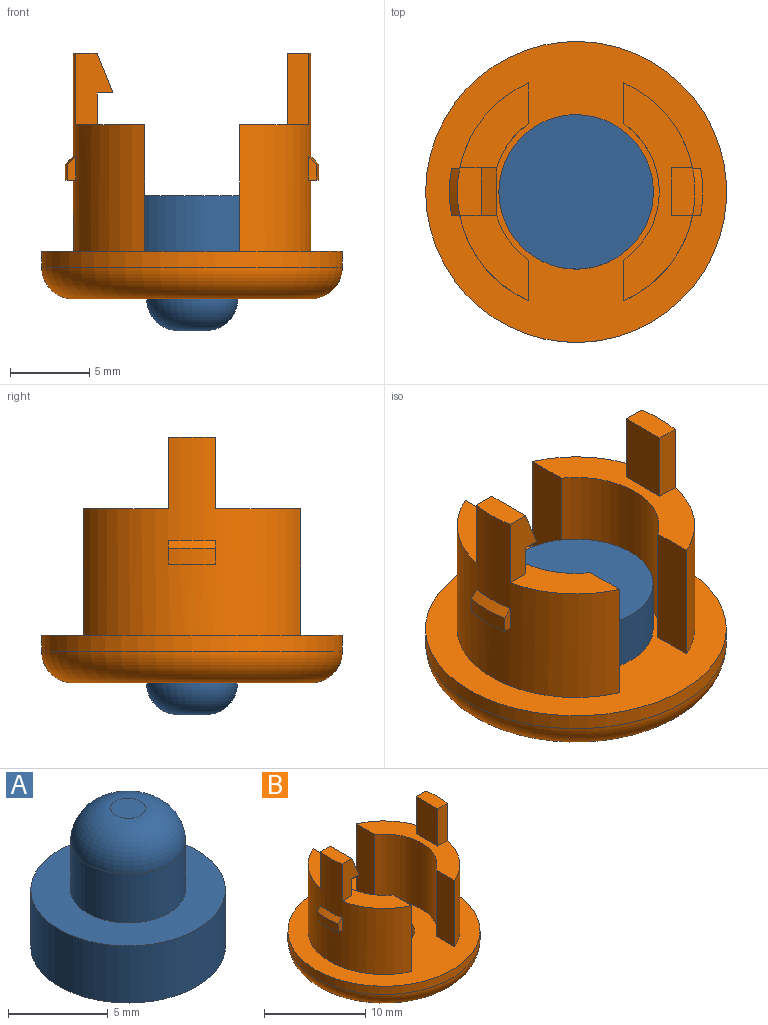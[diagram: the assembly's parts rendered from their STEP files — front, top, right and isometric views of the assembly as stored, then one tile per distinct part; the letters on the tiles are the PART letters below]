
ASSEMBLY  parts=2 mates=1
PART A: 6 faces, bbox 9.8x9.8x8.5 mm
  f0: cylinder r=4.88mm len=9.75mm, axis (0,0,-1), area 107.2mm2, adj f1,f2
  f1: plane 9.75x9.75mm, normal (0,0,1), area 48.7mm2, adj f0,f3
  f2: plane 9.75x9.75mm, normal (0,0,-1), area 74.7mm2, adj f0
  f3: cylinder r=2.88mm len=5.75mm, axis (0,0,-1), area 54.2mm2, adj f1,f5
  f4: plane 1.75x1.75mm, normal (0,0,1), area 2.4mm2, adj f5
  f5: torus R=0.88mm, axis (0,0,1), area 42.4mm2, adj f3,f4
PART B: 35 faces, bbox 20.6x20.6x15.5 mm
  f0: plane 3x2mm, normal (1,0,0), area 6mm2, adj f2,f26,f27,f33
  f1: plane 13.75x4.35mm, normal (0,0,1), area 26.6mm2, adj f3,f4,f12,f14,f29,f30,f31
  f2: plane 13.75x4.35mm, normal (0,0,1), area 26.6mm2, adj f0,f5,f6,f13,f15,f26,f27
  f3: cylinder r=5.25mm len=8.62mm, axis (0,0,-1), area 80.9mm2, adj f1,f7,f12,f14
  f4: cylinder r=7.5mm len=13.75mm, axis (0,0,-1), area 148.2mm2, adj f1,f7,f12,f14,f20,f21,f23,f24
  f5: cylinder r=5.25mm len=8.62mm, axis (0,0,-1), area 80.9mm2, adj f2,f7,f13,f15
  f6: cylinder r=7.5mm len=13.75mm, axis (0,0,-1), area 148.2mm2, adj f2,f7,f13,f15,f16,f18,f19,f25
  f7: plane 19x19mm, normal (0,0,1), area 193.3mm2, adj f3,f4,f5,f6,f8,f9,f12,f13
  f8: cylinder r=9.5mm len=19mm, axis (0,0,1), area 59.7mm2, adj f7,f11
  f9: cylinder r=3mm len=6mm, axis (0,0,1), area 56.5mm2, adj f7,f10
  f10: plane 15x15mm, normal (0,0,-1), area 148.4mm2, adj f9,f11
  f11: torus R=7.5mm, axis (0,0,-1), area 173.2mm2, adj f8,f10
  f12: plane 8x2.57mm, normal (-1,0,0), area 20.5mm2, adj f1,f3,f4,f7
  f13: plane 8x2.57mm, normal (1,0,0), area 20.5mm2, adj f2,f5,f6,f7
  f14: plane 8x2.57mm, normal (-1,0,0), area 20.5mm2, adj f1,f3,f4,f7
  f15: plane 8x2.57mm, normal (1,0,0), area 20.5mm2, adj f2,f5,f6,f7
  f16: plane 1.5x0.51mm, normal (0,1,0), area 0.6mm2, adj f6,f17,f19,f25
  f17: cylinder r=8mm len=3mm, axis (0,0,-1), area 3mm2, adj f16,f18,f19,f25
  f18: plane 1.5x0.51mm, normal (0,-1,0), area 0.6mm2, adj f6,f17,f19,f25
  f19: plane 3x0.65mm, normal (0,0,-1), area 1.5mm2, adj f6,f16,f17,f18
  f20: plane 1.5x0.51mm, normal (0,1,0), area 0.6mm2, adj f4,f22,f23,f24
  f21: plane 1.5x0.51mm, normal (0,-1,0), area 0.6mm2, adj f4,f22,f23,f24
  f22: cylinder r=8mm len=3mm, axis (0,0,-1), area 3mm2, adj f20,f21,f23,f24
  f23: plane 3x0.65mm, normal (0,0,-1), area 1.5mm2, adj f4,f20,f21,f22
  f24: cone r=7.5mm half-angle=45deg, axis (0,0,-1), area 2.1mm2, adj f4,f20,f21,f22
  f25: cone r=7.5mm half-angle=45deg, axis (0,0,-1), area 2.1mm2, adj f6,f16,f17,f18
  f26: plane 4.5x2.35mm, normal (0,1,0), area 7.3mm2, adj f0,f2,f6,f28,f33,f34
  f27: plane 4.5x2.35mm, normal (0,-1,0), area 7.3mm2, adj f0,f2,f6,f28,f33,f34
  f28: plane 3x1.5mm, normal (0,0,1), area 4.3mm2, adj f6,f26,f27,f34
  f29: plane 4.5x1.35mm, normal (0,-1,0), area 6.1mm2, adj f1,f4,f31,f32
  f30: plane 4.5x1.35mm, normal (0,1,0), area 6.1mm2, adj f1,f4,f31,f32
  f31: plane 4.5x3mm, normal (-1,0,0), area 13.5mm2, adj f1,f29,f30,f32
  f32: plane 3x1.5mm, normal (0,0,1), area 4.3mm2, adj f4,f29,f30,f31
  f33: plane 3x1mm, normal (0,0,-1), area 3mm2, adj f0,f26,f27,f34
  f34: plane 3x2.5mm, normal (0.93,0,0.37), area 8.1mm2, adj f26,f27,f28,f33
PLACE A rot(axis=(0,1,0),180deg) t=(0,0,6.5)mm
PLACE B t=(0,0,3)mm
MATE fastened A.f3 <-> B.f9  axis (0,0,-1) through (0,0,3)mm
